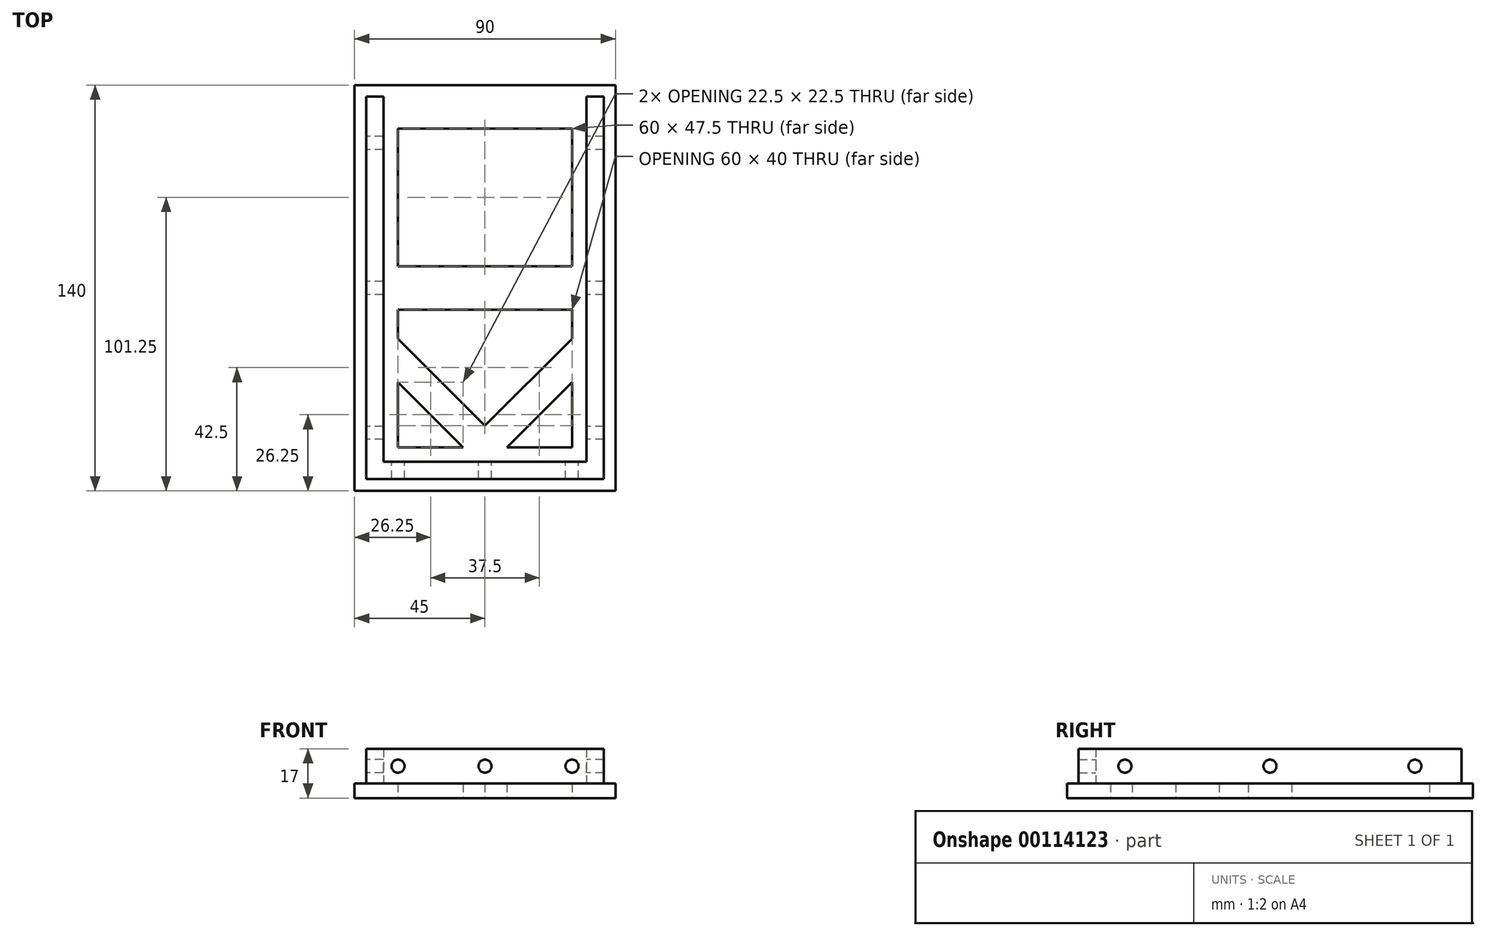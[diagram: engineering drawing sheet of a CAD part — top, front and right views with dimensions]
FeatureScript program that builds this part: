
annotation { "Feature Type Name" : "Feature", "Feature Type Description" : "" }
export const myFeature = defineFeature(function(context is Context, id is Id, definition is map)
    precondition{}
    {
        {
            var Q0;
            Q0=qCreatedBy(makeId("Top.planeOp"),FACE);
            var sketch = newSketch(context, id + "F0", { "sketchPlane" : qUnion([Q0])});
            skLineSegment(sketch, "E0.bottom", {"start": v(-45, 70) * mm, "end": v(45, 70) * mm});
            skLineSegment(sketch, "E0.top", {"start": v(-45, -70) * mm, "end": v(45, -70) * mm});
            skLineSegment(sketch, "E0.left", {"start": v(-45, 70) * mm, "end": v(-45, -70) * mm});
            skLineSegment(sketch, "E0.right", {"start": v(45, 70) * mm, "end": v(45, -70) * mm});
            skPoint(sketch, "E0.middle", {"position": v(0, 0) * mm});
            skLineSegment(sketch, "E1.bottom", {"start": v(-30, 55) * mm, "end": v(30, 55) * mm});
            skLineSegment(sketch, "E1.top", {"start": v(-30, -55) * mm, "end": v(30, -55) * mm});
            skLineSegment(sketch, "E1.left", {"start": v(-30, 55) * mm, "end": v(-30, -55) * mm});
            skLineSegment(sketch, "E1.right", {"start": v(30, 55) * mm, "end": v(30, -55) * mm});
            skLineSegment(sketch, "E2", {"start": v(0, 55) * mm, "end": v(0, -55) * mm, "construction": true});
            skLineSegment(sketch, "E3", {"start": v(-30, 0) * mm, "end": v(30, 0) * mm, "construction": true});
            skLineSegment(sketch, "E4", {"start": v(-7.5, 55) * mm, "end": v(7.5, 55) * mm});
            skLineSegment(sketch, "E5", {"start": v(-7.5, 55) * mm, "end": v(-30, 32.5) * mm});
            skLineSegment(sketch, "E6", {"start": v(7.5, 55) * mm, "end": v(30, 32.5) * mm});
            skLineSegment(sketch, "E7", {"start": v(-30, 17.5) * mm, "end": v(0, 47.5) * mm});
            skLineSegment(sketch, "E8", {"start": v(0, 47.5) * mm, "end": v(30, 17.5) * mm});
            skLineSegment(sketch, "E9", {"start": v(-7.5, -55) * mm, "end": v(-30, -32.5) * mm});
            skLineSegment(sketch, "E10", {"start": v(7.5, -55) * mm, "end": v(30, -32.5) * mm});
            skLineSegment(sketch, "E11", {"start": v(-30, -17.5) * mm, "end": v(0, -47.5) * mm});
            skLineSegment(sketch, "E12", {"start": v(0, -47.5) * mm, "end": v(30, -17.5) * mm});
            skLineSegment(sketch, "E13", {"start": v(-30, 7.5) * mm, "end": v(30, 7.5) * mm});
            skLineSegment(sketch, "E14", {"start": v(30, 7.5) * mm, "end": v(30, -7.5) * mm});
            skLineSegment(sketch, "E15", {"start": v(30, -7.5) * mm, "end": v(-30, -7.5) * mm});
            skSolve(sketch);
        }
        {
            var Q0;
            Q0=makeQuery(id+"F0.imprint","IMPRINT",FACE,{"disambiguationData":[TD([[makeQuery(id+"F0.imprint","IMPRINT",EDGE,{"derivedFrom":sQuery(id+"F0.wireOp",EDGE,"E0.bottom")}),-1.0]])]});
            var Q1;
            Q1=makeQuery(id+"F0.imprint","IMPRINT",FACE,{"disambiguationData":[TD([[makeQuery(id+"F0.imprint","IMPRINT",EDGE,{"derivedFrom":sQuery(id+"F0.wireOp",EDGE,"E4")}),-1.0]])]});
            var Q2;
            {var subQ0=sQuery(id+"F0.wireOp",EDGE,"E9");Q2=makeQuery(id+"F0.imprint","IMPRINT",FACE,{"disambiguationData":[TD([[makeQuery(id+"F0.imprint","IMPRINT",EDGE,{"derivedFrom":subQ0}),-1.0]])]});}
            var Q3;
            {var subQ0=sQuery(id+"F0.wireOp",EDGE,"E13");Q3=makeQuery(id+"F0.imprint","IMPRINT",FACE,{"disambiguationData":[TD([[makeQuery(id+"F0.imprint","IMPRINT",EDGE,{"derivedFrom":subQ0}),-1.0]])]});}
            extrude(context, id + "F1", {"entities" : qUnion([Q0, Q1, Q2, Q3]), "depth" : 5 * mm});
        }
        {
            var Q0;
            Q0=makeQuery(id+"F1.opExtrude","CAP_FACE",FACE,{"disambiguationData":[OSD([sQuery(id+"F0.wireOp",EDGE,"E0.bottom"),sQuery(id+"F0.wireOp",EDGE,"E0.top"),sQuery(id+"F0.wireOp",EDGE,"E0.left"),sQuery(id+"F0.wireOp",EDGE,"E0.right"),sQuery(id+"F0.wireOp",EDGE,"E1.bottom"),sQuery(id+"F0.wireOp",EDGE,"E1.top"),sQuery(id+"F0.wireOp",EDGE,"E1.left"),sQuery(id+"F0.wireOp",EDGE,"E1.right"),sQuery(id+"F0.wireOp",EDGE,"E5"),sQuery(id+"F0.wireOp",EDGE,"E6"),sQuery(id+"F0.wireOp",EDGE,"E7"),sQuery(id+"F0.wireOp",EDGE,"E8"),sQuery(id+"F0.wireOp",EDGE,"E9"),sQuery(id+"F0.wireOp",EDGE,"E10"),sQuery(id+"F0.wireOp",EDGE,"E11"),sQuery(id+"F0.wireOp",EDGE,"E12"),sQuery(id+"F0.wireOp",EDGE,"E13"),sQuery(id+"F0.wireOp",EDGE,"E15")])],"isStart":false});
            var sketch = newSketch(context, id + "F2", { "sketchPlane" : qUnion([Q0])});
            skLineSegment(sketch, "E16.bottom", {"start": v(-35, 60) * mm, "end": v(35, 60) * mm});
            skLineSegment(sketch, "E16.top", {"start": v(-35, -60) * mm, "end": v(35, -60) * mm});
            skLineSegment(sketch, "E16.left", {"start": v(-35, 60) * mm, "end": v(-35, -60) * mm});
            skLineSegment(sketch, "E16.right", {"start": v(35, 60) * mm, "end": v(35, -60) * mm});
            skPoint(sketch, "E16.middle", {"position": v(0, 0) * mm});
            skLineSegment(sketch, "E17.bottom", {"start": v(-41, 66) * mm, "end": v(41, 66) * mm});
            skLineSegment(sketch, "E17.top", {"start": v(-41, -66) * mm, "end": v(41, -66) * mm});
            skLineSegment(sketch, "E17.left", {"start": v(-41, 66) * mm, "end": v(-41, -66) * mm});
            skLineSegment(sketch, "E17.right", {"start": v(41, 66) * mm, "end": v(41, -66) * mm});
            skSolve(sketch);
        }
        {
            var Q0;
            Q0=makeQuery(id+"F2.imprint","IMPRINT",FACE,{"disambiguationData":[TD([[makeQuery(id+"F2.imprint","IMPRINT",EDGE,{"derivedFrom":sQuery(id+"F2.wireOp",EDGE,"E16.bottom")}),1.0]])]});
            extrude(context, id + "F3", {"entities" : qUnion([Q0]), "operationType" : NewBodyOperationType.ADD, "depth" : 12 * mm});
        }
        {
            var Q0;
            Q0=makeQuery(id+"F3.opExtrude","SWEPT_FACE",FACE,{"disambiguationData":[OSD([sQuery(id+"F2.wireOp",EDGE,"E17.left")])]});
            var sketch = newSketch(context, id + "F4", { "sketchPlane" : qUnion([Q0])});
            skPoint(sketch, "E18", {"position": v(-66, 11) * mm});
            skPoint(sketch, "E19", {"position": v(66, 11) * mm});
            skCircle(sketch, "E20", {"center": v(-50, 11) * mm, "radius": 2.25 * mm});
            skCircle(sketch, "E21", {"center": v(50, 11) * mm, "radius": 2.25 * mm});
            skCircle(sketch, "E22", {"center": v(0, 11) * mm, "radius": 2.25 * mm});
            skSolve(sketch);
        }
        {
            var Q0;
            Q0=makeQuery(id+"F4.imprint","IMPRINT",FACE,{"disambiguationData":[TD([[makeQuery(id+"F4.imprint","IMPRINT",EDGE,{"derivedFrom":sQuery(id+"F4.wireOp",EDGE,"E20")}),1.0]])]});
            var Q1;
            Q1=makeQuery(id+"F4.imprint","IMPRINT",FACE,{"disambiguationData":[TD([[makeQuery(id+"F4.imprint","IMPRINT",EDGE,{"derivedFrom":sQuery(id+"F4.wireOp",EDGE,"E22")}),1.0]])]});
            var Q2;
            Q2=makeQuery(id+"F4.imprint","IMPRINT",FACE,{"disambiguationData":[TD([[makeQuery(id+"F4.imprint","IMPRINT",EDGE,{"derivedFrom":sQuery(id+"F4.wireOp",EDGE,"E21")}),1.0]])]});
            extrude(context, id + "F5", {"entities" : qUnion([Q0, Q1, Q2]), "operationType" : NewBodyOperationType.REMOVE, "endBound" : BoundingType.THROUGH_ALL, "oppositeDirection" : true, "depth" : 25 * mm});
        }
        {
            var Q0;
            Q0=makeQuery(id+"F3.opExtrude","SWEPT_FACE",FACE,{"disambiguationData":[OSD([sQuery(id+"F2.wireOp",EDGE,"E17.bottom")])]});
            var sketch = newSketch(context, id + "F6", { "sketchPlane" : qUnion([Q0])});
            skPoint(sketch, "E23", {"position": v(-41, 11) * mm});
            skCircle(sketch, "E24", {"center": v(-30, 11) * mm, "radius": 2.25 * mm});
            skCircle(sketch, "E25", {"center": v(0, 11) * mm, "radius": 2.25 * mm});
            skCircle(sketch, "E26", {"center": v(30, 11) * mm, "radius": 2.25 * mm});
            skSolve(sketch);
        }
        {
            var Q0;
            Q0=makeQuery(id+"F6.imprint","IMPRINT",FACE,{"disambiguationData":[TD([[makeQuery(id+"F6.imprint","IMPRINT",EDGE,{"derivedFrom":sQuery(id+"F6.wireOp",EDGE,"E24")}),1.0]])]});
            var Q1;
            Q1=makeQuery(id+"F6.imprint","IMPRINT",FACE,{"disambiguationData":[TD([[makeQuery(id+"F6.imprint","IMPRINT",EDGE,{"derivedFrom":sQuery(id+"F6.wireOp",EDGE,"E25")}),1.0]])]});
            var Q2;
            Q2=makeQuery(id+"F6.imprint","IMPRINT",FACE,{"disambiguationData":[TD([[makeQuery(id+"F6.imprint","IMPRINT",EDGE,{"derivedFrom":sQuery(id+"F6.wireOp",EDGE,"E26")}),1.0]])]});
            extrude(context, id + "F7", {"entities" : qUnion([Q0, Q1, Q2]), "operationType" : NewBodyOperationType.REMOVE, "endBound" : BoundingType.THROUGH_ALL, "oppositeDirection" : true, "depth" : 25 * mm});
        }
        {
            var Q0;
            Q0=makeQuery(id+"F3.opExtrude","SWEPT_FACE",FACE,{"disambiguationData":[OSD([sQuery(id+"F2.wireOp",EDGE,"E17.bottom")])]});
            var sketch = newSketch(context, id + "F8", { "sketchPlane" : qUnion([Q0])});
            skLineSegment(sketch, "E27.0", {"start": v(-35, 17) * mm, "end": v(-35, 5) * mm});
            skLineSegment(sketch, "E28.0", {"start": v(35, 17) * mm, "end": v(35, 5) * mm});
            skSolve(sketch);
        }
        {
            var Q0;
            {var subQ1=sQuery(id+"F8.wireOp",EDGE,"E27.0");Q0=makeQuery(id+"F8.imprint","IMPRINT",FACE,{"disambiguationData":[TD([[makeQuery(id+"F8.imprint","IMPRINT",EDGE,{"derivedFrom":subQ1}),1.0]])]});}
            extrude(context, id + "F9", {"entities" : qUnion([Q0]), "operationType" : NewBodyOperationType.REMOVE, "endBound" : BoundingType.UP_TO_NEXT, "oppositeDirection" : true, "depth" : 25 * mm});
        }
    });
